# Revit family: AVS 200
name_source: partatom
category: Mechanical Equipment
units: mm (PartAtom-declared; Revit-internal decimal feet)

## family parameters
Always vertical = No
Classification = None
Cut with Voids When Loaded = No
Maintain Annotation Orientation = No
OmniClass Number = 23.75.35.17.11
OmniClass Title = Fans for Air Ductwork
Part Type = Breaks Into
Room Calculation Point = No
Round Connector Dimension = Use Diameter
Shared = No
Work Plane-Based = No

## types (6) — shared parameters
Dd12 = 1 mm  [stored 0.00328084 ft]
Dd13 = 2 mm  [stored 0.00656168 ft]
Distribution Box Material = Distribution Box Dark Grey
ElBoxH = 53 mm  [stored 0.173885 ft]
ElBoxL = 104 mm
ElBoxR = 15 mm  [stored 0.0492126 ft]
ElBoxW = 104 mm
Family Version = 1.0
Fan Material = Metal Black
Hanger Material = Metal Zinc
HangerExtraL = No
L14 = 10 mm  [stored 0.0328084 ft]
L16 = 6 mm  [stored 0.019685 ft]
L22 = 8 mm  [stored 0.0262467 ft]
L23 = 13 mm
L26 = 6 mm  [stored 0.019685 ft]
Load Classification = HVAC
Maintenance Zone Height = 600 mm
Maintenance Zone Length = 600 mm
Maintenance Zone Material = Maintenance Zone
Maintenance Zone Width = 600 mm
Manufacturer = Vents
Number of Poles = 1
Power Factor = 1
Protection rating = IPX4
Transported Air Temperature (°C) = -25...+60
Voltage = 230 V
zero-valued in all types: Default Elevation

## per-type parameters (varying)
- TT Silent-M 200 (min): Apparent Power=78 VA; Current=0 A; D=200 mm  [stored 0.656168 ft]; D1=293 mm; Dd14=9 mm  [stored 0.0295276 ft]; Dd16=44 mm  [stored 0.144357 ft]; Dd22=4 mm  [stored 0.0131234 ft]; Dd23=5 mm  [stored 0.0164042 ft]; Dd24=27 mm  [stored 0.0885827 ft]; Dd26=44 mm  [stored 0.144357 ft]; Description=Inline mixed-flow fan in sound- and heat-insulated casing for round ducts; Duct Connection Size=200 mm  [stored 0.656168 ft]; HangerBaseH=149 mm  [stored 0.488845 ft]; HangerH=149 mm  [stored 0.488845 ft]; HangerL=344 mm; HangerL1=275 mm; HangerW=135 mm  [stored 0.442913 ft]; L=550 mm; L1=30 mm  [stored 0.0984252 ft]; L11=148 mm  [stored 0.485564 ft]; L12=3 mm  [stored 0.00984252 ft]; L13=4 mm  [stored 0.0131234 ft]; L15=116 mm  [stored 0.380577 ft]; L17=9 mm  [stored 0.0295276 ft]; L2=30 mm  [stored 0.0984252 ft]; L21=179 mm  [stored 0.58727 ft]; L24=21 mm  [stored 0.0688976 ft]; L25=122 mm; L27=9 mm  [stored 0.0295276 ft]; Maintenance Zone Length Calc=600 mm; Maximum Air Flow=810 m³/h; Model=TT Silent-M 200; Noise Level at 3 m (dBa)=31; Power=78 W; R1=147 mm; RPM (min-1)=2015; Type Comments=Inline mixed-flow fan TT Silent-M 200; URL=https://ventilation-system.com; Weight=8.00 kg
- Aventa Silent AVS200: Apparent Power=110 VA; Current=0 A; D=200 mm  [stored 0.656168 ft]; D1=293 mm; Dd14=9 mm  [stored 0.0295276 ft]; Dd16=44 mm  [stored 0.144357 ft]; Dd22=4 mm  [stored 0.0131234 ft]; Dd23=5 mm  [stored 0.0164042 ft]; Dd24=27 mm  [stored 0.0885827 ft]; Dd26=44 mm  [stored 0.144357 ft]; Description=Inline mixed-flow fan suitable for domestic and light commercial facilities; Duct Connection Size=200 mm  [stored 0.656168 ft]; HangerBaseH=149 mm  [stored 0.488845 ft]; HangerH=149 mm  [stored 0.488845 ft]; HangerL=344 mm; HangerL1=275 mm; HangerW=135 mm  [stored 0.442913 ft]; L=550 mm; L1=30 mm  [stored 0.0984252 ft]; L11=148 mm  [stored 0.485564 ft]; L12=3 mm  [stored 0.00984252 ft]; L13=4 mm  [stored 0.0131234 ft]; L15=116 mm  [stored 0.380577 ft]; L17=9 mm  [stored 0.0295276 ft]; L2=30 mm  [stored 0.0984252 ft]; L21=179 mm  [stored 0.58727 ft]; L24=21 mm  [stored 0.0688976 ft]; L25=122 mm; L27=9 mm  [stored 0.0295276 ft]; Maintenance Zone Length Calc=600 mm; Maximum Air Flow=1020 m³/h; Model=Aventa Silent AVS200; Noise Level at 3 m (dBa)=36; Power=110 W; R1=147 mm; RPM (min-1)=2445; Type Comments=Inline fan single speed up to 1020m3/h; URL=https://www.airflow.com; Weight=8.00 kg
- TT Silent-M 250 (min): Apparent Power=125 VA; Current=1 A; D=250 mm; D1=358 mm; Dd14=6 mm  [stored 0.019685 ft]; Dd16=52 mm; Dd22=5 mm  [stored 0.0164042 ft]; Dd23=6 mm  [stored 0.019685 ft]; Dd24=30 mm  [stored 0.0984252 ft]; Dd26=52 mm; Description=Inline mixed-flow fan in sound- and heat-insulated casing for round ducts; Duct Connection Size=250 mm; HangerBaseH=182 mm  [stored 0.597113 ft]; HangerH=182 mm  [stored 0.597113 ft]; HangerL=402 mm; HangerL1=332 mm; HangerW=150 mm; L=658 mm; L1=32 mm  [stored 0.104987 ft]; L11=176 mm  [stored 0.577428 ft]; L12=3 mm  [stored 0.00984252 ft]; L13=4 mm  [stored 0.0131234 ft]; L15=144 mm  [stored 0.472441 ft]; L17=9 mm  [stored 0.0295276 ft]; L2=32 mm  [stored 0.104987 ft]; L21=218 mm  [stored 0.715223 ft]; L24=23 mm  [stored 0.0754593 ft]; L25=159 mm; L27=9 mm  [stored 0.0295276 ft]; Maintenance Zone Length Calc=658 mm; Maximum Air Flow=1110 m³/h; Model=TT Silent-M 250; Noise Level at 3 m (dBa)=34; Power=125 W; R1=179 mm  [stored 0.58727 ft]; RPM (min-1)=1955; Type Comments=Inline mixed-flow fan TT Silent-M 250; URL=https://ventilation-system.com; Weight=15.00 kg
- TT Silent-M 250 (max): Apparent Power=177 VA; Current=1 A; D=250 mm; D1=358 mm; Dd14=6 mm  [stored 0.019685 ft]; Dd16=52 mm; Dd22=5 mm  [stored 0.0164042 ft]; Dd23=6 mm  [stored 0.019685 ft]; Dd24=30 mm  [stored 0.0984252 ft]; Dd26=52 mm; Description=Inline mixed-flow fan in sound- and heat-insulated casing for round ducts; Duct Connection Size=250 mm; HangerBaseH=182 mm  [stored 0.597113 ft]; HangerH=182 mm  [stored 0.597113 ft]; HangerL=402 mm; HangerL1=332 mm; HangerW=150 mm; L=658 mm; L1=32 mm  [stored 0.104987 ft]; L11=176 mm  [stored 0.577428 ft]; L12=3 mm  [stored 0.00984252 ft]; L13=4 mm  [stored 0.0131234 ft]; L15=144 mm  [stored 0.472441 ft]; L17=9 mm  [stored 0.0295276 ft]; L2=32 mm  [stored 0.104987 ft]; L21=218 mm  [stored 0.715223 ft]; L24=23 mm  [stored 0.0754593 ft]; L25=159 mm; L27=9 mm  [stored 0.0295276 ft]; Maintenance Zone Length Calc=658 mm; Maximum Air Flow=1400 m³/h; Model=TT Silent-M 250; Noise Level at 3 m (dBa)=38; Power=177 W; R1=179 mm  [stored 0.58727 ft]; RPM (min-1)=2440; Type Comments=Inline mixed-flow fan TT Silent-M 250; URL=https://ventilation-system.com; Weight=15.00 kg
- TT Silent-M 315 (min): Apparent Power=230 VA; Current=1 A; D=315 mm; D1=432 mm; Dd14=6 mm  [stored 0.019685 ft]; Dd16=55 mm  [stored 0.180446 ft]; Dd22=5 mm  [stored 0.0164042 ft]; Dd23=6 mm  [stored 0.019685 ft]; Dd24=30 mm  [stored 0.0984252 ft]; Dd26=52 mm; Description=Inline mixed-flow fan in sound- and heat-insulated casing for round ducts; Duct Connection Size=315 mm; HangerBaseH=219 mm; HangerH=219 mm; HangerL=478 mm; HangerL1=396 mm; HangerW=200 mm  [stored 0.656168 ft]; L=780 mm; L1=32 mm  [stored 0.104987 ft]; L11=195 mm  [stored 0.639764 ft]; L12=8 mm  [stored 0.0262467 ft]; L13=8 mm  [stored 0.0262467 ft]; L15=153 mm  [stored 0.501969 ft]; L17=10 mm  [stored 0.0328084 ft]; L2=32 mm  [stored 0.104987 ft]; L21=218 mm  [stored 0.715223 ft]; L24=27 mm  [stored 0.0885827 ft]; L25=154 mm; L27=10 mm  [stored 0.0328084 ft]; Maintenance Zone Length Calc=780 mm; Maximum Air Flow=1570 m³/h; Model=TT Silent-M 315; Noise Level at 3 m (dBa)=36; Power=230 W; R1=216 mm  [stored 0.708661 ft]; RPM (min-1)=1890; Type Comments=Inline mixed-flow fan TT Silent-M 315; URL=https://ventilation-system.com; Weight=25.00 kg
- TT Silent-M 315 (max): Apparent Power=320 VA; Current=1 A; D=315 mm; D1=432 mm; Dd14=6 mm  [stored 0.019685 ft]; Dd16=55 mm  [stored 0.180446 ft]; Dd22=5 mm  [stored 0.0164042 ft]; Dd23=6 mm  [stored 0.019685 ft]; Dd24=30 mm  [stored 0.0984252 ft]; Dd26=52 mm; Description=Inline mixed-flow fan in sound- and heat-insulated casing for round ducts; Duct Connection Size=315 mm; HangerBaseH=219 mm; HangerH=219 mm; HangerL=478 mm; HangerL1=396 mm; HangerW=200 mm  [stored 0.656168 ft]; L=780 mm; L1=32 mm  [stored 0.104987 ft]; L11=195 mm  [stored 0.639764 ft]; L12=8 mm  [stored 0.0262467 ft]; L13=8 mm  [stored 0.0262467 ft]; L15=153 mm  [stored 0.501969 ft]; L17=10 mm  [stored 0.0328084 ft]; L2=32 mm  [stored 0.104987 ft]; L21=218 mm  [stored 0.715223 ft]; L24=27 mm  [stored 0.0885827 ft]; L25=154 mm; L27=10 mm  [stored 0.0328084 ft]; Maintenance Zone Length Calc=780 mm; Maximum Air Flow=2050 m³/h; Model=TT Silent-M 315; Noise Level at 3 m (dBa)=40; Power=320 W; R1=216 mm  [stored 0.708661 ft]; RPM (min-1)=2430; Type Comments=Inline mixed-flow fan TT Silent-M 315; URL=https://ventilation-system.com; Weight=25.00 kg

note: [stored X ft] marks values corroborated as IEEE doubles in the binary element streams (Revit-internal decimal feet)

## geometry (parser evidence)
native form markers: Sweep x11
no freeform markers — native parametric forms only
